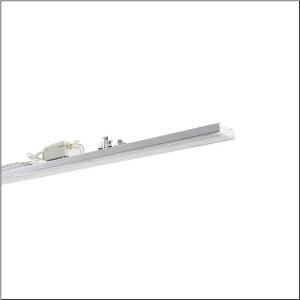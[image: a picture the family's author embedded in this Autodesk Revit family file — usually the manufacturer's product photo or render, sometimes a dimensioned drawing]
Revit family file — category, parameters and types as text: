
# Revit family: licross_r__11_recessed_mo_51tl12dn4axg3c_2e33
name_source: partatom
category: Lighting Fixtures
units: mm (PartAtom-declared; Revit-internal decimal feet)

## family parameters
Cut with Voids When Loaded = No
Host = Face
Light Source = No
Part Type = Normal
Room Calculation Point = No
Round Connector Dimension = Use Diameter
Shared = No

## types (1)
- --- (1 x LED, 1010 lm, 6.7 W, 4000K)
    Apparent Load = 7 VA
    CIE Flux Codes = 67 92 99 100 100
    Color Rendering = 80
    Color Temperature = 4000K
    Default Elevation = 1800 mm
    Description = Licross® 11 Recessed MO, luminaire insert, of sheet steel, coil coated, white, length: 1.500mm, width: 66mm, height: 67mm, LED rated luminous flux: 10.240lm, light colour: 840, control gear: DALI 2 (for two DALI lines), with plug, 6-pole, with phase selection, for trunking rail, 14-core, mains connection: 220..240V, AC, 50/60Hz, rated input power: 61W, for trunking rail, 14-core, halogen-free wiring, for emergency light function, converter,control gear: single battery element, battery: LiFePO4, 9Ah, primary optical cover: cover, of PMMA, light emission: direct distribution, primary light characteristic: symmetric, protection rating (complete): IP40, insulation class (complete): insulation class I (protective earthing), certification: CE, UKCA, protection symbol: D if used in an environment without relevant dust loads with corresponding accessories, impact resistance: IK06, permissible ambient temperature for indoor applications: +5..+35°C, standard: EN 60598-2-22, LABS conformity tested according to VDMA 24364:2018-05, reducing of maximum allowable ambient temperature of 5°C with ceiling mounting, corresponds to IFS (International Featured Standards) requirements for safety and quality in the food industry, packaging unit: 1 piece
    Height = 58 mm
    Lamp = 1 x LED
    Lamp Light Flux = 1010 lm
    Lamp Power = 6.7 W
    Lamp count = 1
    Length = 1500 mm
    Luminous efficacy = 151 lm/W
    Manufacturer = Siteco
    ModVariant = No
    Model = 51TL12DN4AXG3C
    Mounting Place = Ceiling
    Mounting Type = Pendant
    Number of Poles = 1
    OnlyDefault = Yes
    Power Factor = 1
    Product Name = Licross® 11 Recessed MO
    Product group = luminaire insert
    ProductGroupID = 901
    Protection Class = Protection class I
    Protection Degree = IP 40
    RLX_Detail_Level = 1
    RLX_Emergency_Light_Flux = 0 lm
    RLX_Emergency_Type = 0
    RLX_Emergency_Type_DB = No
    RlxData = <blob elided: 24785 chars, md5=79b15fd4>
    Socket = socket
    Standby Power = 0 W
    System Light Flux = 1010 lm
    System Power = 7 W
    Type Comments = : emergency light operation: 3 h
    Type Image = l_1296930.jpg
    URL = http://relux.com
    VarID = @adj_059025
    Voltage = 0 V
    Weight = 0.00 kg
    Width = 66 mm

## geometry (parser evidence)
native form markers: Blend x4, Sweep x11
no freeform markers — native parametric forms only
